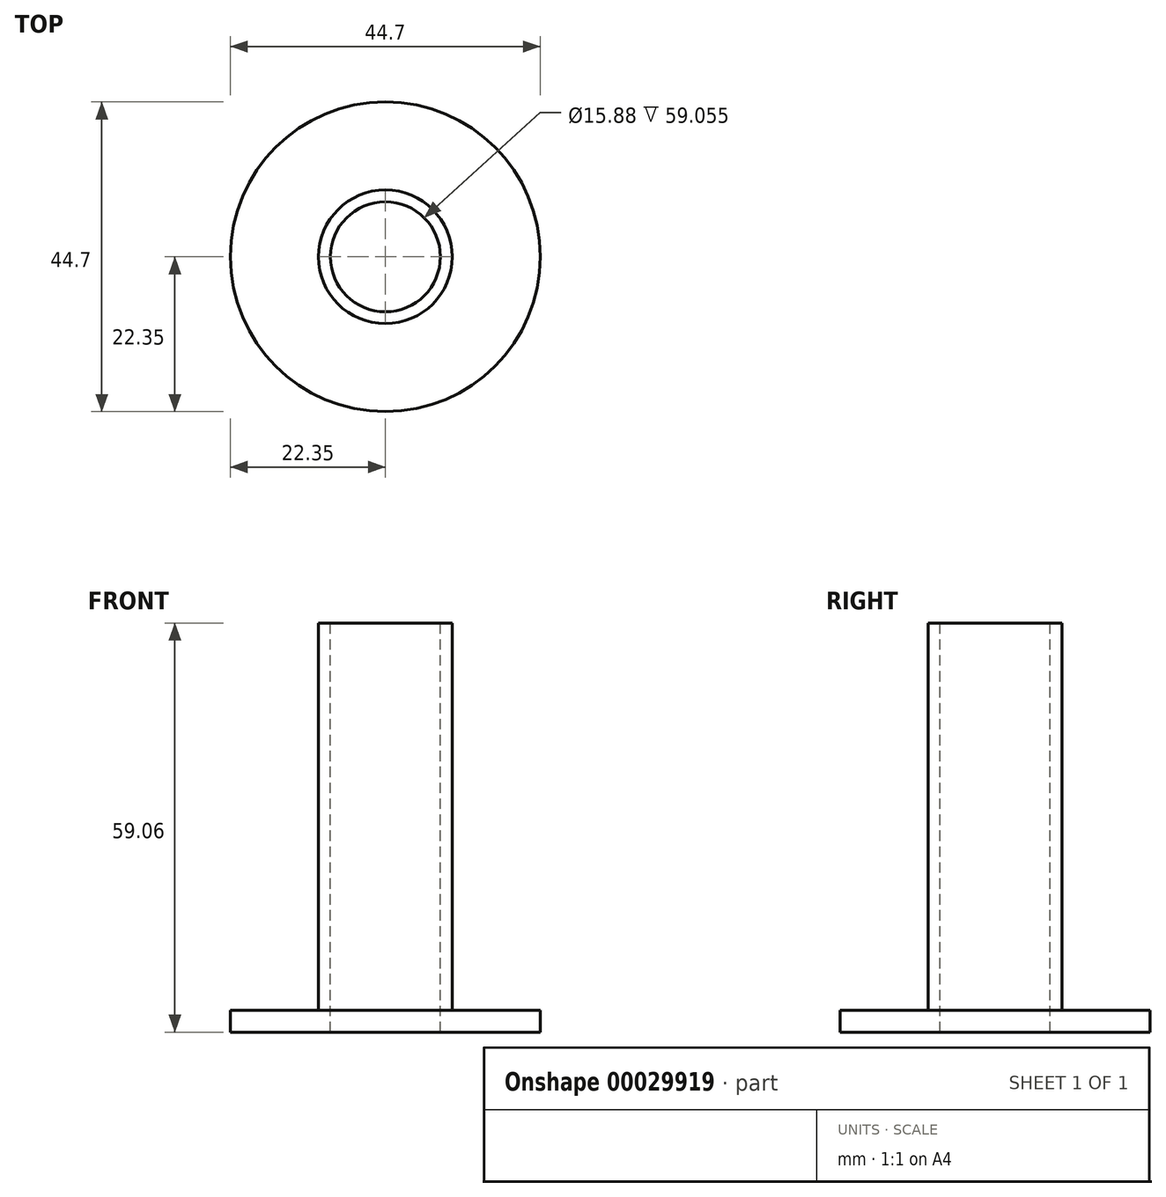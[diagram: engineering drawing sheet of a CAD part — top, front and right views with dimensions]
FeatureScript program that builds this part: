
annotation { "Feature Type Name" : "Feature", "Feature Type Description" : "" }
export const myFeature = defineFeature(function(context is Context, id is Id, definition is map)
    precondition{}
    {
        {
            var Q0;
            Q0=qCreatedBy(makeId("Front.planeOp"),FACE);
            var sketch = newSketch(context, id + "F0", { "sketchPlane" : qUnion([Q0])});
            skLineSegment(sketch, "E0", {"start": v(7.94, 29.53) * mm, "end": v(7.94, -29.53) * mm});
            skLineSegment(sketch, "E1", {"start": v(7.94, -29.53) * mm, "end": v(22.35, -29.53) * mm});
            skLineSegment(sketch, "E2", {"start": v(22.35, -29.53) * mm, "end": v(22.35, -26.35) * mm});
            skLineSegment(sketch, "E3", {"start": v(22.35, -26.35) * mm, "end": v(9.65, -26.35) * mm});
            skLineSegment(sketch, "E4", {"start": v(9.65, -26.35) * mm, "end": v(9.65, 29.53) * mm});
            skLineSegment(sketch, "E5", {"start": v(9.65, 29.53) * mm, "end": v(7.94, 29.53) * mm});
            skPoint(sketch, "E6", {"position": v(7.94, 0) * mm});
            skLineSegment(sketch, "E7", {"start": v(0, 29.53) * mm, "end": v(0, -29.53) * mm, "construction": true});
            skSolve(sketch);
        }
        {
            var Q0;
            Q0 = qSketchRegion(id + "F0", true);
            var Q1;
            Q1=sQuery(id+"F0.wireOp",EDGE,"E7");
            revolve(context, id + "F1", {"entities" : qUnion([Q0]), "axis" : qUnion([Q1]), "revolveType" : RevolveType.FULL});
        }
    });
